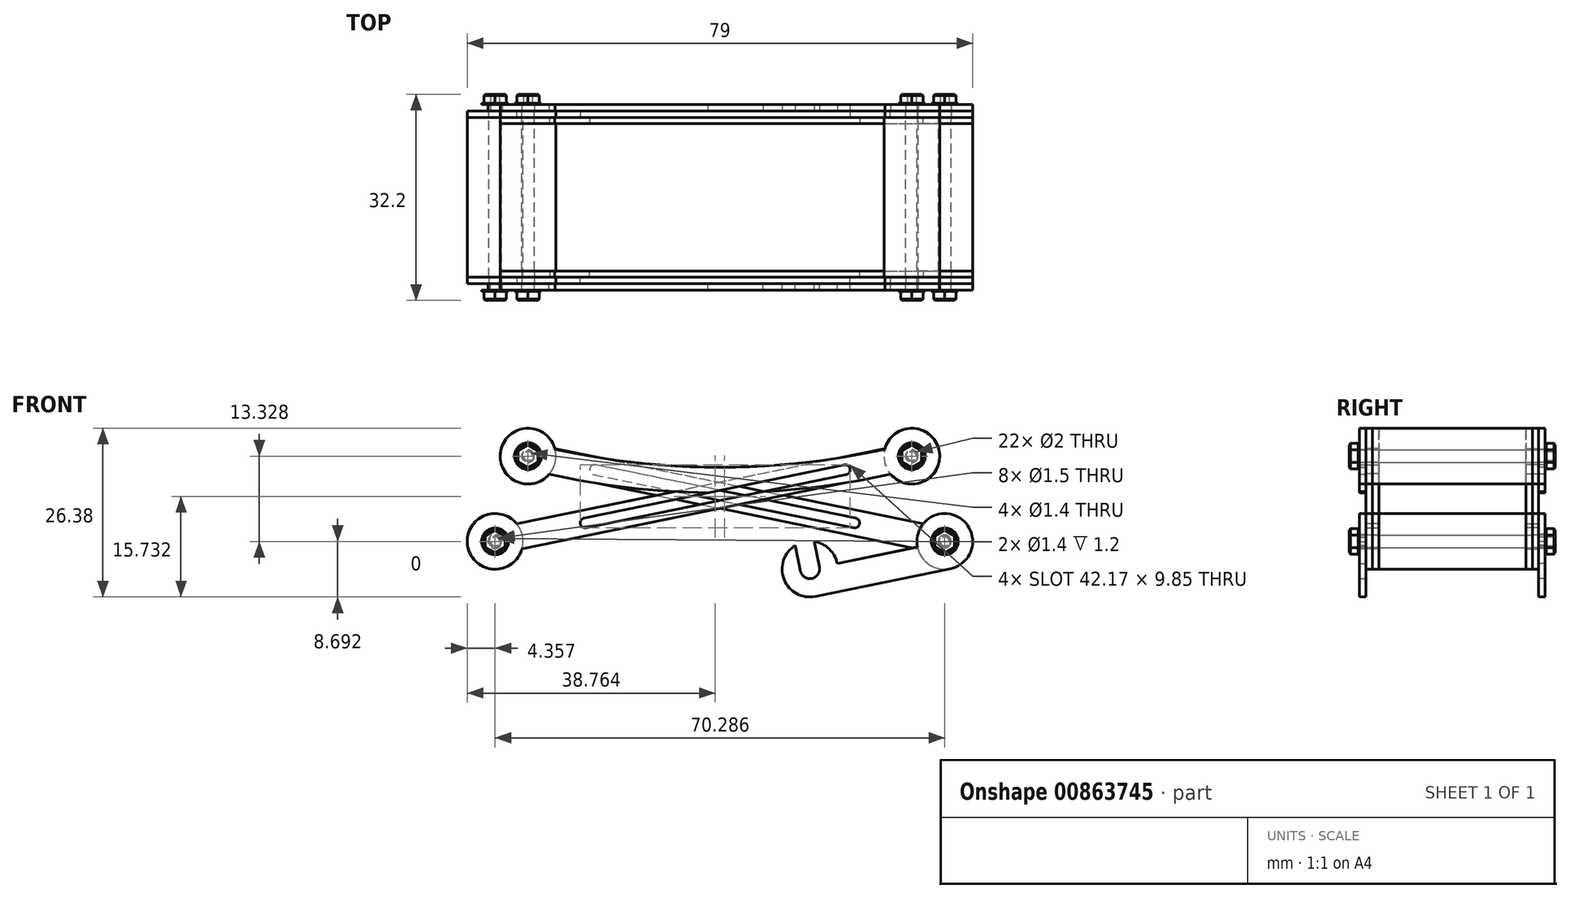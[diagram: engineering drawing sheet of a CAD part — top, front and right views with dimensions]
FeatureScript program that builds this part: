
annotation { "Feature Type Name" : "Feature", "Feature Type Description" : "" }
export const myFeature = defineFeature(function(context is Context, id is Id, definition is map)
    precondition{}
    {
        {
            var Q0;
            Q0=qCreatedBy(makeId("Front.planeOp"),FACE);
            var sketch = newSketch(context, id + "F0", { "sketchPlane" : qUnion([Q0])});
            skLineSegment(sketch, "E0", {"start": v(0, 0) * mm, "end": v(-30, 40) * mm, "construction": true});
            skLineSegment(sketch, "E1", {"start": v(-30, 40) * mm, "end": v(30, 40) * mm, "construction": true});
            skLineSegment(sketch, "E2", {"start": v(30, 40) * mm, "end": v(0, 0) * mm, "construction": true});
            skLineSegment(sketch, "E3", {"start": v(0, 0) * mm, "end": v(0, 40) * mm, "construction": true});
            skArc(sketch, "E4", {"start": v(-30, 40) * mm, "mid": v(0, 36.26) * mm, "end": v(30, 40) * mm, "construction": true});
            skPoint(sketch, "E4.third.point", {"position": v(0, 36.26) * mm});
            skLineSegment(sketch, "E5", {"start": v(30, 40) * mm, "end": v(-35.14, 26.67) * mm, "construction": true});
            skSolve(sketch);
        }
        {
            var Q0;
            Q0=qCreatedBy(makeId("Front.planeOp"),FACE);
            var sketch = newSketch(context, id + "F1", { "sketchPlane" : qUnion([Q0])});
            skArc(sketch, "E6", {"start": v(-25.77, 41.06) * mm, "mid": v(-34.24, 41) * mm, "end": v(-26.7, 37.16) * mm});
            skArc(sketch, "E7", {"start": v(26.7, 37.16) * mm, "mid": v(34.24, 41) * mm, "end": v(25.77, 41.06) * mm});
            skArc(sketch, "E8.0", {"start": v(-26.7, 37.16) * mm, "mid": v(0, 34.26) * mm, "end": v(26.7, 37.16) * mm});
            skArc(sketch, "E9.0", {"start": v(-25.77, 41.06) * mm, "mid": v(0, 38.26) * mm, "end": v(25.77, 41.06) * mm});
            skCircle(sketch, "E10", {"center": v(30, 40) * mm, "radius": 1 * mm});
            skCircle(sketch, "E11", {"center": v(-30, 40) * mm, "radius": 1 * mm});
            skSolve(sketch);
        }
        {
            var Q0;
            Q0=qCreatedBy(makeId("Front.planeOp"),FACE);
            var sketch = newSketch(context, id + "F2", { "sketchPlane" : qUnion([Q0])});
            skCircle(sketch, "E12", {"center": v(30, 40) * mm, "radius": 4.36 * mm});
            skLineSegment(sketch, "E13.0", {"start": v(29.6, 41.96) * mm, "end": v(-31.75, 29.4) * mm});
            skLineSegment(sketch, "E14.0", {"start": v(30.4, 38.04) * mm, "end": v(-30.95, 25.49) * mm});
            skArc(sketch, "E15", {"start": v(-31.75, 29.4) * mm, "mid": v(-39.41, 25.8) * mm, "end": v(-30.95, 25.49) * mm});
            skCircle(sketch, "E16", {"center": v(30, 40) * mm, "radius": 1 * mm});
            skCircle(sketch, "E17", {"center": v(-35.14, 26.67) * mm, "radius": 1 * mm});
            skSolve(sketch);
        }
        {
            var Q0;
            Q0 = qSketchRegion(id + "F2", true);
            extrude(context, id + "F3", {"entities" : qUnion([Q0]), "depth" : 1 * mm, "offsetDistance" : 25 * mm});
        }
        {
            var Q0;
            Q0 = qSketchRegion(id + "F1", true);
            extrude(context, id + "F4", {"entities" : qUnion([Q0]), "oppositeDirection" : true, "depth" : 1 * mm, "offsetDistance" : 25 * mm});
        }
        {
            var Q0;
            Q0=makeQuery(id+"F3.opExtrude","CAP_FACE",FACE,{"disambiguationData":[OSD([sQuery(id+"F2.wireOp",EDGE,"E12"),sQuery(id+"F2.wireOp",EDGE,"E13.0"),sQuery(id+"F2.wireOp",EDGE,"E14.0"),sQuery(id+"F2.wireOp",EDGE,"E15"),sQuery(id+"F2.wireOp",EDGE,"E16"),sQuery(id+"F2.wireOp",EDGE,"E17")])],"isStart":false});
            var sketch = newSketch(context, id + "F5", { "sketchPlane" : qUnion([Q0])});
            skCircle(sketch, "E18", {"center": v(30, 40) * mm, "radius": 4.36 * mm});
            skCircle(sketch, "E19", {"center": v(30, 40) * mm, "radius": 1 * mm});
            skCircle(sketch, "E20", {"center": v(-35.14, 26.67) * mm, "radius": 4.36 * mm});
            skCircle(sketch, "E21", {"center": v(-35.14, 26.67) * mm, "radius": 1 * mm});
            skSolve(sketch);
        }
        {
            var Q0;
            Q0 = qSketchRegion(id + "F5", true);
            extrude(context, id + "F6", {"entities" : qUnion([Q0]), "depth" : 25 * mm, "offsetDistance" : 25 * mm});
        }
        {
            var Q0;
            Q0=makeQuery(id+"F4.opExtrude","CAP_FACE",FACE,{"disambiguationData":[OSD([sQuery(id+"F1.wireOp",EDGE,"E6"),sQuery(id+"F1.wireOp",EDGE,"E7"),sQuery(id+"F1.wireOp",EDGE,"E8.0"),sQuery(id+"F1.wireOp",EDGE,"E9.0"),sQuery(id+"F1.wireOp",EDGE,"E10"),sQuery(id+"F1.wireOp",EDGE,"E11")])],"isStart":true});
            var sketch = newSketch(context, id + "F7", { "sketchPlane" : qUnion([Q0])});
            skCircle(sketch, "E22", {"center": v(-30, 40) * mm, "radius": 4.36 * mm});
            skCircle(sketch, "E23", {"center": v(-30, 40) * mm, "radius": 1 * mm});
            skSolve(sketch);
        }
        {
            var Q0;
            Q0 = qSketchRegion(id + "F7", true);
            extrude(context, id + "F8", {"entities" : qUnion([Q0]), "depth" : 1 * mm, "offsetDistance" : 25 * mm});
        }
        {
            var Q0;
            Q0=makeQuery(id+"F8.opExtrude","CAP_FACE",FACE,{"disambiguationData":[OSD([sQuery(id+"F7.wireOp",EDGE,"E22"),sQuery(id+"F7.wireOp",EDGE,"E23")])],"isStart":false});
            var sketch = newSketch(context, id + "F9", { "sketchPlane" : qUnion([Q0])});
            skSolve(sketch);
        }
        {
            var Q0;
            Q0=makeQuery(id+"F3.opExtrude","CAP_FACE",FACE,{"disambiguationData":[OSD([sQuery(id+"F2.wireOp",EDGE,"E12"),sQuery(id+"F2.wireOp",EDGE,"E13.0"),sQuery(id+"F2.wireOp",EDGE,"E14.0"),sQuery(id+"F2.wireOp",EDGE,"E15"),sQuery(id+"F2.wireOp",EDGE,"E16"),sQuery(id+"F2.wireOp",EDGE,"E17")])],"isStart":false});
            var sketch = newSketch(context, id + "F10", { "sketchPlane" : qUnion([Q0])});
            skLineSegment(sketch, "E24", {"start": v(-35.14, 26.67) * mm, "end": v(30, 40) * mm, "construction": true});
            skArc(sketch, "E25", {"start": v(-21.2, 30.32) * mm, "mid": v(-21.82, 29.4) * mm, "end": v(-20.9, 28.79) * mm});
            skArc(sketch, "E26", {"start": v(19.74, 37.1) * mm, "mid": v(20.35, 38.02) * mm, "end": v(19.42, 38.63) * mm});
            skLineSegment(sketch, "E27", {"start": v(-21.05, 29.56) * mm, "end": v(-0.74, 33.71) * mm, "construction": true});
            skLineSegment(sketch, "E28", {"start": v(-0.74, 33.71) * mm, "end": v(19.58, 37.87) * mm, "construction": true});
            skLineSegment(sketch, "E29", {"start": v(-21.2, 30.32) * mm, "end": v(19.42, 38.63) * mm});
            skLineSegment(sketch, "E30", {"start": v(19.74, 37.1) * mm, "end": v(-20.9, 28.79) * mm});
            skLineSegment(sketch, "E31", {"start": v(-21.2, 30.32) * mm, "end": v(-20.9, 28.79) * mm, "construction": true});
            skLineSegment(sketch, "E32", {"start": v(19.42, 38.63) * mm, "end": v(19.74, 37.1) * mm, "construction": true});
            skSolve(sketch);
        }
        {
            var Q0;
            Q0 = qSketchRegion(id + "F10", true);
            extrude(context, id + "F11", {"entities" : qUnion([Q0]), "operationType" : NewBodyOperationType.REMOVE, "oppositeDirection" : true, "depth" : 2 * mm, "offsetDistance" : 25 * mm});
        }
        {
            var Q0;
            Q0=makeQuery(id+"F3.opExtrude","SWEPT_BODY",BODY,{"disambiguationData":[OSD([sQuery(id+"F2.wireOp",EDGE,"E12"),sQuery(id+"F2.wireOp",EDGE,"E13.0"),sQuery(id+"F2.wireOp",EDGE,"E14.0"),sQuery(id+"F2.wireOp",EDGE,"E15"),sQuery(id+"F2.wireOp",EDGE,"E16"),sQuery(id+"F2.wireOp",EDGE,"E17")])]});
            var Q1;
            Q1=qCreatedBy(makeId("Right.planeOp"),FACE);
            mirror(context, id + "F12", {"entities" : qUnion([Q0]), "mirrorPlane" : qUnion([Q1])});
        }
        {
            var Q0;
            Q0=makeQuery(id+"F12.opPattern","COPY",BODY,{"derivedFrom":makeQuery(id+"F3.opExtrude","SWEPT_BODY",BODY,{"disambiguationData":[OSD([sQuery(id+"F2.wireOp",EDGE,"E12"),sQuery(id+"F2.wireOp",EDGE,"E13.0"),sQuery(id+"F2.wireOp",EDGE,"E14.0"),sQuery(id+"F2.wireOp",EDGE,"E15"),sQuery(id+"F2.wireOp",EDGE,"E16"),sQuery(id+"F2.wireOp",EDGE,"E17")])]}),"instanceName":"1"});
            var Q1;
            Q1=makeQuery(id+"F6.opExtrude","CAP_FACE",FACE,{"disambiguationData":[OSD([sQuery(id+"F5.wireOp",EDGE,"E20"),sQuery(id+"F5.wireOp",EDGE,"E21")])],"isStart":false});
            transform(context, id + "F13", {"entities" : qUnion([Q0]), "transformType" : TransformType.TRANSLATION_DISTANCE, "transformDirection" : qUnion([Q1]), "distance" : 1 * mm, "makeCopy" : false});
        }
        {
            var Q0;
            Q0=makeQuery(id+"F9.imprint","IMPRINT",FACE,{"disambiguationData":[TD([[makeQuery(id+"F9.imprint","IMPRINT",EDGE,{"derivedFrom":makeQuery(id+"F8.opExtrude","CAP_EDGE",EDGE,{"disambiguationData":[OSD([sQuery(id+"F7.wireOp",EDGE,"E22")])],"isStart":false})}),1.0]])]});
            extrude(context, id + "F14", {"entities" : qUnion([Q0]), "depth" : 24 * mm, "offsetDistance" : 25 * mm, "hasSecondDirection" : true, "secondDirectionOppositeDirection" : true, "secondDirectionDepth" : -1 * mm});
        }
        {
            var Q0;
            Q0=qCreatedBy(makeId("Front.planeOp"),FACE);
            cPlane(context, id + "F15", {"entities" : qUnion([Q0]), "cplaneType" : CPlaneType.OFFSET, "offset" : 13.5 * mm, "width" : 150 * mm, "height" : 150 * mm});
        }
        {
            var Q0;
            Q0=makeQuery(id+"F12.opPattern","COPY",BODY,{"derivedFrom":makeQuery(id+"F3.opExtrude","SWEPT_BODY",BODY,{"disambiguationData":[OSD([sQuery(id+"F2.wireOp",EDGE,"E12"),sQuery(id+"F2.wireOp",EDGE,"E13.0"),sQuery(id+"F2.wireOp",EDGE,"E14.0"),sQuery(id+"F2.wireOp",EDGE,"E15"),sQuery(id+"F2.wireOp",EDGE,"E16"),sQuery(id+"F2.wireOp",EDGE,"E17")])]}),"instanceName":"1"});
            var Q1;
            Q1=makeQuery(id+"F4.opExtrude","SWEPT_BODY",BODY,{"disambiguationData":[OSD([sQuery(id+"F1.wireOp",EDGE,"E6"),sQuery(id+"F1.wireOp",EDGE,"E7"),sQuery(id+"F1.wireOp",EDGE,"E8.0"),sQuery(id+"F1.wireOp",EDGE,"E9.0"),sQuery(id+"F1.wireOp",EDGE,"E10"),sQuery(id+"F1.wireOp",EDGE,"E11")])]});
            var Q2;
            Q2=makeQuery(id+"F8.opExtrude","SWEPT_BODY",BODY,{"disambiguationData":[OSD([sQuery(id+"F7.wireOp",EDGE,"E22"),sQuery(id+"F7.wireOp",EDGE,"E23")])]});
            var Q3;
            Q3=makeQuery(id+"F3.opExtrude","SWEPT_BODY",BODY,{"disambiguationData":[OSD([sQuery(id+"F2.wireOp",EDGE,"E12"),sQuery(id+"F2.wireOp",EDGE,"E13.0"),sQuery(id+"F2.wireOp",EDGE,"E14.0"),sQuery(id+"F2.wireOp",EDGE,"E15"),sQuery(id+"F2.wireOp",EDGE,"E16"),sQuery(id+"F2.wireOp",EDGE,"E17")])]});
            var Q4;
            Q4=qCreatedBy(id+"F15.planeOp",FACE);
            mirror(context, id + "F16", {"entities" : qUnion([Q0, Q1, Q2, Q3]), "mirrorPlane" : qUnion([Q4])});
        }
        {
            var Q0;
            Q0=makeQuery(id+"F12.opPattern","COPY",FACE,{"derivedFrom":makeQuery(id+"F3.opExtrude","CAP_FACE",FACE,{"disambiguationData":[OSD([sQuery(id+"F2.wireOp",EDGE,"E12"),sQuery(id+"F2.wireOp",EDGE,"E13.0"),sQuery(id+"F2.wireOp",EDGE,"E14.0"),sQuery(id+"F2.wireOp",EDGE,"E15"),sQuery(id+"F2.wireOp",EDGE,"E16"),sQuery(id+"F2.wireOp",EDGE,"E17")])],"isStart":false}),"instanceName":"1"});
            var sketch = newSketch(context, id + "F17", { "sketchPlane" : qUnion([Q0])});
            skCircle(sketch, "E33", {"center": v(35.14, 26.67) * mm, "radius": 4.36 * mm});
            skCircle(sketch, "E34", {"center": v(35.14, 26.67) * mm, "radius": 1 * mm});
            skSolve(sketch);
        }
        {
            var Q0;
            Q0 = qSketchRegion(id + "F17", true);
            var Q1;
            Q1=makeQuery(id+"F16.opPattern","COPY",FACE,{"derivedFrom":makeQuery(id+"F12.opPattern","COPY",FACE,{"derivedFrom":makeQuery(id+"F3.opExtrude","CAP_FACE",FACE,{"disambiguationData":[OSD([sQuery(id+"F2.wireOp",EDGE,"E12"),sQuery(id+"F2.wireOp",EDGE,"E13.0"),sQuery(id+"F2.wireOp",EDGE,"E14.0"),sQuery(id+"F2.wireOp",EDGE,"E15"),sQuery(id+"F2.wireOp",EDGE,"E16"),sQuery(id+"F2.wireOp",EDGE,"E17")])],"isStart":false}),"instanceName":"1"}),"instanceName":"1"});
            extrude(context, id + "F18", {"entities" : qUnion([Q0]), "endBound" : BoundingType.UP_TO_SURFACE, "depth" : 25 * mm, "endBoundEntityFace" : qUnion([Q1]), "offsetDistance" : 25 * mm});
        }
        {
            var Q0;
            Q0=makeQuery(id+"F12.opPattern","COPY",FACE,{"derivedFrom":makeQuery(id+"F3.opExtrude","CAP_FACE",FACE,{"disambiguationData":[OSD([sQuery(id+"F2.wireOp",EDGE,"E12"),sQuery(id+"F2.wireOp",EDGE,"E13.0"),sQuery(id+"F2.wireOp",EDGE,"E14.0"),sQuery(id+"F2.wireOp",EDGE,"E15"),sQuery(id+"F2.wireOp",EDGE,"E16"),sQuery(id+"F2.wireOp",EDGE,"E17")])],"isStart":true}),"instanceName":"1"});
            var sketch = newSketch(context, id + "F19", { "sketchPlane" : qUnion([Q0])});
            skCircle(sketch, "E35", {"center": v(-35.14, 26.67) * mm, "radius": 4.36 * mm});
            skCircle(sketch, "E36", {"center": v(-35.14, 26.67) * mm, "radius": 1 * mm});
            skSolve(sketch);
        }
        {
            var Q0;
            Q0 = qSketchRegion(id + "F19", true);
            extrude(context, id + "F20", {"entities" : qUnion([Q0]), "depth" : 1 * mm, "offsetDistance" : 25 * mm});
        }
        {
            var Q0;
            Q0=makeQuery(id+"F20.opExtrude","SWEPT_BODY",BODY,{"disambiguationData":[OSD([sQuery(id+"F19.wireOp",EDGE,"E35"),sQuery(id+"F19.wireOp",EDGE,"E36")])]});
            var Q1;
            Q1=qCreatedBy(id+"F15.planeOp",FACE);
            mirror(context, id + "F21", {"entities" : qUnion([Q0]), "mirrorPlane" : qUnion([Q1])});
        }
        {
            var Q0;
            Q0=makeQuery(id+"F21.opPattern","COPY",FACE,{"derivedFrom":makeQuery(id+"F20.opExtrude","CAP_FACE",FACE,{"disambiguationData":[OSD([sQuery(id+"F19.wireOp",EDGE,"E35"),sQuery(id+"F19.wireOp",EDGE,"E36")])],"isStart":false}),"instanceName":"1"});
            var sketch = newSketch(context, id + "F22", { "sketchPlane" : qUnion([Q0])});
            skArc(sketch, "E37", {"start": v(36.02, 22.4) * mm, "mid": v(37.54, 30.31) * mm, "end": v(30.88, 25.8) * mm});
            skLineSegment(sketch, "E38", {"start": v(35.14, 26.67) * mm, "end": v(36.02, 22.4) * mm, "construction": true});
            skLineSegment(sketch, "E39", {"start": v(36.02, 22.4) * mm, "end": v(14.96, 18.07) * mm, "construction": true});
            skLineSegment(sketch, "E40", {"start": v(35.14, 26.67) * mm, "end": v(14.08, 22.34) * mm, "construction": true});
            skLineSegment(sketch, "E41", {"start": v(14.08, 22.34) * mm, "end": v(14.96, 18.07) * mm, "construction": true});
            skArc(sketch, "E42", {"start": v(11.78, 26.04) * mm, "mid": v(10.03, 20.73) * mm, "end": v(14.96, 18.07) * mm});
            skArc(sketch, "E43", {"start": v(12.6, 22.04) * mm, "mid": v(14.38, 20.87) * mm, "end": v(15.55, 22.64) * mm});
            skLineSegment(sketch, "E44", {"start": v(15.55, 22.64) * mm, "end": v(14.72, 26.65) * mm});
            skLineSegment(sketch, "E45", {"start": v(12.6, 22.04) * mm, "end": v(11.78, 26.04) * mm});
            skLineSegment(sketch, "E46", {"start": v(11.78, 26.04) * mm, "end": v(14.72, 26.65) * mm, "construction": true});
            skLineSegment(sketch, "E47", {"start": v(14.08, 22.34) * mm, "end": v(12.6, 22.04) * mm, "construction": true});
            skArc(sketch, "E48.trimOffspring", {"start": v(18.35, 23.22) * mm, "mid": v(17.07, 25.5) * mm, "end": v(14.72, 26.65) * mm});
            skLineSegment(sketch, "E49", {"start": v(18.35, 23.22) * mm, "end": v(30.88, 25.8) * mm});
            skLineSegment(sketch, "E50", {"start": v(14.96, 18.07) * mm, "end": v(36.02, 22.4) * mm});
            skCircle(sketch, "E51", {"center": v(35.14, 26.67) * mm, "radius": 1 * mm});
            skSolve(sketch);
        }
        {
            var Q0;
            Q0 = qSketchRegion(id + "F22", true);
            extrude(context, id + "F23", {"entities" : qUnion([Q0]), "depth" : 1 * mm, "offsetDistance" : 25 * mm});
        }
        {
            var Q0;
            Q0=makeQuery(id+"F23.opExtrude","SWEPT_BODY",BODY,{"disambiguationData":[OSD([sQuery(id+"F22.wireOp",EDGE,"E37"),sQuery(id+"F22.wireOp",EDGE,"E42"),sQuery(id+"F22.wireOp",EDGE,"E43"),sQuery(id+"F22.wireOp",EDGE,"E44"),sQuery(id+"F22.wireOp",EDGE,"E45"),sQuery(id+"F22.wireOp",EDGE,"E48.trimOffspring"),sQuery(id+"F22.wireOp",EDGE,"E49"),sQuery(id+"F22.wireOp",EDGE,"E50"),sQuery(id+"F22.wireOp",EDGE,"E51")])]});
            var Q1;
            Q1=qCreatedBy(id+"F15.planeOp",FACE);
            mirror(context, id + "F24", {"entities" : qUnion([Q0]), "mirrorPlane" : qUnion([Q1])});
        }
        {
            var Q0;
            Q0=makeQuery(id+"F16.opPattern","COPY",FACE,{"derivedFrom":makeQuery(id+"F4.opExtrude","CAP_FACE",FACE,{"disambiguationData":[OSD([sQuery(id+"F1.wireOp",EDGE,"E6"),sQuery(id+"F1.wireOp",EDGE,"E7"),sQuery(id+"F1.wireOp",EDGE,"E8.0"),sQuery(id+"F1.wireOp",EDGE,"E9.0"),sQuery(id+"F1.wireOp",EDGE,"E10"),sQuery(id+"F1.wireOp",EDGE,"E11")])],"isStart":false}),"instanceName":"1"});
            var sketch = newSketch(context, id + "F25", { "sketchPlane" : qUnion([Q0])});
            skCircle(sketch, "E52.cCircle", {"center": v(30, 40) * mm, "radius": 2 * mm, "construction": true});
            skLineSegment(sketch, "E52.0", {"start": v(30, 42) * mm, "end": v(31.74, 41) * mm});
            skLineSegment(sketch, "E52.1", {"start": v(31.74, 41) * mm, "end": v(31.73, 39) * mm});
            skLineSegment(sketch, "E52.2", {"start": v(31.73, 39) * mm, "end": v(30, 38) * mm});
            skLineSegment(sketch, "E52.3", {"start": v(30, 38) * mm, "end": v(28.26, 39) * mm});
            skLineSegment(sketch, "E52.4", {"start": v(28.26, 39) * mm, "end": v(28.27, 41) * mm});
            skLineSegment(sketch, "E52.5", {"start": v(28.27, 41) * mm, "end": v(30, 42) * mm});
            skCircle(sketch, "E53.cCircle", {"center": v(35.14, 26.67) * mm, "radius": 2 * mm, "construction": true});
            skLineSegment(sketch, "E53.0", {"start": v(35.15, 28.67) * mm, "end": v(36.88, 27.67) * mm});
            skLineSegment(sketch, "E53.1", {"start": v(36.88, 27.67) * mm, "end": v(36.87, 25.67) * mm});
            skLineSegment(sketch, "E53.2", {"start": v(36.87, 25.67) * mm, "end": v(35.14, 24.67) * mm});
            skLineSegment(sketch, "E53.3", {"start": v(35.14, 24.67) * mm, "end": v(33.4, 25.68) * mm});
            skLineSegment(sketch, "E53.4", {"start": v(33.4, 25.68) * mm, "end": v(33.41, 27.68) * mm});
            skLineSegment(sketch, "E53.5", {"start": v(33.41, 27.68) * mm, "end": v(35.15, 28.67) * mm});
            skSolve(sketch);
        }
        {
            var Q0;
            Q0 = qSketchRegion(id + "F25", true);
            extrude(context, id + "F26", {"entities" : qUnion([Q0]), "depth" : 1.6 * mm, "offsetDistance" : 25 * mm, "hasSecondDirection" : true, "secondDirectionOppositeDirection" : false, "secondDirectionDepth" : .2 * mm});
        }
        {
            var Q0;
            Q0=makeQuery(id+"F26.opExtrude","CAP_EDGE",EDGE,{"disambiguationData":[OSD([sQuery(id+"F25.wireOp",EDGE,"E52.2")])],"isStart":false});
            var Q1;
            Q1=makeQuery(id+"F26.opExtrude","CAP_EDGE",EDGE,{"disambiguationData":[OSD([sQuery(id+"F25.wireOp",EDGE,"E52.1")])],"isStart":false});
            var Q2;
            Q2=makeQuery(id+"F26.opExtrude","CAP_EDGE",EDGE,{"disambiguationData":[OSD([sQuery(id+"F25.wireOp",EDGE,"E52.0")])],"isStart":false});
            var Q3;
            Q3=makeQuery(id+"F26.opExtrude","CAP_EDGE",EDGE,{"disambiguationData":[OSD([sQuery(id+"F25.wireOp",EDGE,"E52.5")])],"isStart":false});
            var Q4;
            Q4=makeQuery(id+"F26.opExtrude","CAP_EDGE",EDGE,{"disambiguationData":[OSD([sQuery(id+"F25.wireOp",EDGE,"E52.4")])],"isStart":false});
            var Q5;
            Q5=makeQuery(id+"F26.opExtrude","CAP_EDGE",EDGE,{"disambiguationData":[OSD([sQuery(id+"F25.wireOp",EDGE,"E52.3")])],"isStart":false});
            var Q6;
            Q6=makeQuery(id+"F26.opExtrude","CAP_EDGE",EDGE,{"disambiguationData":[OSD([sQuery(id+"F25.wireOp",EDGE,"E53.0")])],"isStart":false});
            var Q7;
            Q7=makeQuery(id+"F26.opExtrude","CAP_EDGE",EDGE,{"disambiguationData":[OSD([sQuery(id+"F25.wireOp",EDGE,"E53.5")])],"isStart":false});
            var Q8;
            Q8=makeQuery(id+"F26.opExtrude","CAP_EDGE",EDGE,{"disambiguationData":[OSD([sQuery(id+"F25.wireOp",EDGE,"E53.4")])],"isStart":false});
            var Q9;
            Q9=makeQuery(id+"F26.opExtrude","CAP_EDGE",EDGE,{"disambiguationData":[OSD([sQuery(id+"F25.wireOp",EDGE,"E53.3")])],"isStart":false});
            var Q10;
            Q10=makeQuery(id+"F26.opExtrude","CAP_EDGE",EDGE,{"disambiguationData":[OSD([sQuery(id+"F25.wireOp",EDGE,"E53.2")])],"isStart":false});
            var Q11;
            Q11=makeQuery(id+"F26.opExtrude","CAP_EDGE",EDGE,{"disambiguationData":[OSD([sQuery(id+"F25.wireOp",EDGE,"E53.1")])],"isStart":false});
            chamfer(context, id + "F27", {"entities" : qUnion([Q0, Q1, Q2, Q3, Q4, Q5, Q6, Q7, Q8, Q9, Q10, Q11]), "width" : .2 * mm, "tangentPropagation" : true});
        }
        {
            var Q0;
            Q0=makeQuery(id+"F26.opExtrude","SWEPT_BODY",BODY,{"disambiguationData":[OSD([sQuery(id+"F25.wireOp",EDGE,"E52.0"),sQuery(id+"F25.wireOp",EDGE,"E52.1"),sQuery(id+"F25.wireOp",EDGE,"E52.2"),sQuery(id+"F25.wireOp",EDGE,"E52.3"),sQuery(id+"F25.wireOp",EDGE,"E52.4"),sQuery(id+"F25.wireOp",EDGE,"E52.5")])]});
            var Q1;
            Q1=makeQuery(id+"F26.opExtrude","SWEPT_BODY",BODY,{"disambiguationData":[OSD([sQuery(id+"F25.wireOp",EDGE,"E53.0"),sQuery(id+"F25.wireOp",EDGE,"E53.1"),sQuery(id+"F25.wireOp",EDGE,"E53.2"),sQuery(id+"F25.wireOp",EDGE,"E53.3"),sQuery(id+"F25.wireOp",EDGE,"E53.4"),sQuery(id+"F25.wireOp",EDGE,"E53.5")])]});
            var Q2;
            Q2=qCreatedBy(id+"F15.planeOp",FACE);
            mirror(context, id + "F28", {"entities" : qUnion([Q0, Q1]), "mirrorPlane" : qUnion([Q2])});
        }
        {
            var Q0;
            Q0=makeQuery(id+"F4.opExtrude","CAP_FACE",FACE,{"disambiguationData":[OSD([sQuery(id+"F1.wireOp",EDGE,"E6"),sQuery(id+"F1.wireOp",EDGE,"E7"),sQuery(id+"F1.wireOp",EDGE,"E8.0"),sQuery(id+"F1.wireOp",EDGE,"E9.0"),sQuery(id+"F1.wireOp",EDGE,"E10"),sQuery(id+"F1.wireOp",EDGE,"E11")])],"isStart":false});
            var sketch = newSketch(context, id + "F29", { "sketchPlane" : qUnion([Q0])});
            skCircle(sketch, "E54", {"center": v(-30, 40) * mm, "radius": 0.7 * mm});
            skCircle(sketch, "E55", {"center": v(-35.14, 26.67) * mm, "radius": 0.7 * mm});
            skSolve(sketch);
        }
        {
            var Q0;
            Q0 = qSketchRegion(id + "F29", true);
            extrude(context, id + "F30", {"entities" : qUnion([Q0]), "operationType" : NewBodyOperationType.REMOVE, "depth" : 25 * mm, "offsetDistance" : 25 * mm});
        }
        {
            var Q0;
            Q0=makeQuery(id+"F30.boolean.opBoolean","INTERSECT",EDGE,{"derivedFrom":[makeQuery(id+"F28.opPattern","COPY",FACE,{"derivedFrom":makeQuery(id+"F26.opExtrude","CAP_FACE",FACE,{"disambiguationData":[OSD([sQuery(id+"F25.wireOp",EDGE,"E52.0"),sQuery(id+"F25.wireOp",EDGE,"E52.1"),sQuery(id+"F25.wireOp",EDGE,"E52.2"),sQuery(id+"F25.wireOp",EDGE,"E52.3"),sQuery(id+"F25.wireOp",EDGE,"E52.4"),sQuery(id+"F25.wireOp",EDGE,"E52.5")])],"isStart":false}),"instanceName":"1"}),makeQuery(id+"F30.opExtrude","SWEPT_FACE",FACE,{"disambiguationData":[OSD([sQuery(id+"F29.wireOp",EDGE,"E54")])]})]});
            var Q1;
            Q1=makeQuery(id+"F30.boolean.opBoolean","INTERSECT",EDGE,{"derivedFrom":[makeQuery(id+"F28.opPattern","COPY",FACE,{"derivedFrom":makeQuery(id+"F26.opExtrude","CAP_FACE",FACE,{"disambiguationData":[OSD([sQuery(id+"F25.wireOp",EDGE,"E53.0"),sQuery(id+"F25.wireOp",EDGE,"E53.1"),sQuery(id+"F25.wireOp",EDGE,"E53.2"),sQuery(id+"F25.wireOp",EDGE,"E53.3"),sQuery(id+"F25.wireOp",EDGE,"E53.4"),sQuery(id+"F25.wireOp",EDGE,"E53.5")])],"isStart":false}),"instanceName":"1"}),makeQuery(id+"F30.opExtrude","SWEPT_FACE",FACE,{"disambiguationData":[OSD([sQuery(id+"F29.wireOp",EDGE,"E55")])]})]});
            chamfer(context, id + "F31", {"entities" : qUnion([Q0, Q1]), "width" : .2 * mm, "tangentPropagation" : true});
        }
        {
            var Q0;
            Q0=makeQuery(id+"F16.opPattern","COPY",FACE,{"derivedFrom":makeQuery(id+"F4.opExtrude","CAP_FACE",FACE,{"disambiguationData":[OSD([sQuery(id+"F1.wireOp",EDGE,"E6"),sQuery(id+"F1.wireOp",EDGE,"E7"),sQuery(id+"F1.wireOp",EDGE,"E8.0"),sQuery(id+"F1.wireOp",EDGE,"E9.0"),sQuery(id+"F1.wireOp",EDGE,"E10"),sQuery(id+"F1.wireOp",EDGE,"E11")])],"isStart":false}),"instanceName":"1"});
            var sketch = newSketch(context, id + "F32", { "sketchPlane" : qUnion([Q0])});
            skCircle(sketch, "E56", {"center": v(30, 40) * mm, "radius": 2.1 * mm});
            skCircle(sketch, "E57", {"center": v(30, 40) * mm, "radius": 0.75 * mm});
            skCircle(sketch, "E58", {"center": v(35.14, 26.67) * mm, "radius": 2.1 * mm});
            skCircle(sketch, "E59", {"center": v(35.14, 26.67) * mm, "radius": 0.75 * mm});
            skSolve(sketch);
        }
        {
            var Q0;
            Q0 = qSketchRegion(id + "F32", true);
            var Q1;
            Q1=makeQuery(id+"F26.opExtrude","CAP_FACE",FACE,{"disambiguationData":[OSD([sQuery(id+"F25.wireOp",EDGE,"E52.0"),sQuery(id+"F25.wireOp",EDGE,"E52.1"),sQuery(id+"F25.wireOp",EDGE,"E52.2"),sQuery(id+"F25.wireOp",EDGE,"E52.3"),sQuery(id+"F25.wireOp",EDGE,"E52.4"),sQuery(id+"F25.wireOp",EDGE,"E52.5")])],"isStart":true});
            extrude(context, id + "F33", {"entities" : qUnion([Q0]), "endBound" : BoundingType.UP_TO_SURFACE, "depth" : 25 * mm, "endBoundEntityFace" : qUnion([Q1]), "offsetDistance" : 25 * mm});
        }
        {
            var Q0;
            Q0=makeQuery(id+"F33.opExtrude","SWEPT_BODY",BODY,{"disambiguationData":[OSD([sQuery(id+"F32.wireOp",EDGE,"E56"),sQuery(id+"F32.wireOp",EDGE,"E57")])]});
            var Q1;
            Q1=makeQuery(id+"F33.opExtrude","SWEPT_BODY",BODY,{"disambiguationData":[OSD([sQuery(id+"F32.wireOp",EDGE,"E58"),sQuery(id+"F32.wireOp",EDGE,"E59")])]});
            var Q2;
            Q2=qCreatedBy(id+"F15.planeOp",FACE);
            mirror(context, id + "F34", {"entities" : qUnion([Q0, Q1]), "mirrorPlane" : qUnion([Q2])});
        }
        {
            var Q0;
            Q0=makeQuery(id+"F26.opExtrude","SWEPT_BODY",BODY,{"disambiguationData":[OSD([sQuery(id+"F25.wireOp",EDGE,"E52.0"),sQuery(id+"F25.wireOp",EDGE,"E52.1"),sQuery(id+"F25.wireOp",EDGE,"E52.2"),sQuery(id+"F25.wireOp",EDGE,"E52.3"),sQuery(id+"F25.wireOp",EDGE,"E52.4"),sQuery(id+"F25.wireOp",EDGE,"E52.5")])]});
            var Q1;
            Q1=makeQuery(id+"F33.opExtrude","SWEPT_BODY",BODY,{"disambiguationData":[OSD([sQuery(id+"F32.wireOp",EDGE,"E56"),sQuery(id+"F32.wireOp",EDGE,"E57")])]});
            var Q2;
            Q2=makeQuery(id+"F26.opExtrude","SWEPT_BODY",BODY,{"disambiguationData":[OSD([sQuery(id+"F25.wireOp",EDGE,"E53.0"),sQuery(id+"F25.wireOp",EDGE,"E53.1"),sQuery(id+"F25.wireOp",EDGE,"E53.2"),sQuery(id+"F25.wireOp",EDGE,"E53.3"),sQuery(id+"F25.wireOp",EDGE,"E53.4"),sQuery(id+"F25.wireOp",EDGE,"E53.5")])]});
            var Q3;
            Q3=makeQuery(id+"F33.opExtrude","SWEPT_BODY",BODY,{"disambiguationData":[OSD([sQuery(id+"F32.wireOp",EDGE,"E58"),sQuery(id+"F32.wireOp",EDGE,"E59")])]});
            var Q4;
            Q4=makeQuery(id+"F34.opPattern","COPY",BODY,{"derivedFrom":makeQuery(id+"F33.opExtrude","SWEPT_BODY",BODY,{"disambiguationData":[OSD([sQuery(id+"F32.wireOp",EDGE,"E58"),sQuery(id+"F32.wireOp",EDGE,"E59")])]}),"instanceName":"1"});
            var Q5;
            Q5=makeQuery(id+"F28.opPattern","COPY",BODY,{"derivedFrom":makeQuery(id+"F26.opExtrude","SWEPT_BODY",BODY,{"disambiguationData":[OSD([sQuery(id+"F25.wireOp",EDGE,"E53.0"),sQuery(id+"F25.wireOp",EDGE,"E53.1"),sQuery(id+"F25.wireOp",EDGE,"E53.2"),sQuery(id+"F25.wireOp",EDGE,"E53.3"),sQuery(id+"F25.wireOp",EDGE,"E53.4"),sQuery(id+"F25.wireOp",EDGE,"E53.5")])]}),"instanceName":"1"});
            var Q6;
            Q6=makeQuery(id+"F28.opPattern","COPY",BODY,{"derivedFrom":makeQuery(id+"F26.opExtrude","SWEPT_BODY",BODY,{"disambiguationData":[OSD([sQuery(id+"F25.wireOp",EDGE,"E52.0"),sQuery(id+"F25.wireOp",EDGE,"E52.1"),sQuery(id+"F25.wireOp",EDGE,"E52.2"),sQuery(id+"F25.wireOp",EDGE,"E52.3"),sQuery(id+"F25.wireOp",EDGE,"E52.4"),sQuery(id+"F25.wireOp",EDGE,"E52.5")])]}),"instanceName":"1"});
            var Q7;
            Q7=makeQuery(id+"F34.opPattern","COPY",BODY,{"derivedFrom":makeQuery(id+"F33.opExtrude","SWEPT_BODY",BODY,{"disambiguationData":[OSD([sQuery(id+"F32.wireOp",EDGE,"E56"),sQuery(id+"F32.wireOp",EDGE,"E57")])]}),"instanceName":"1"});
            var Q8;
            Q8=qCreatedBy(makeId("Right.planeOp"),FACE);
            mirror(context, id + "F35", {"entities" : qUnion([Q0, Q1, Q2, Q3, Q4, Q5, Q6, Q7]), "mirrorPlane" : qUnion([Q8])});
        }
        {
            var Q0;
            Q0=makeQuery(id+"F3.opExtrude","CAP_FACE",FACE,{"disambiguationData":[OSD([sQuery(id+"F2.wireOp",EDGE,"E12"),sQuery(id+"F2.wireOp",EDGE,"E13.0"),sQuery(id+"F2.wireOp",EDGE,"E14.0"),sQuery(id+"F2.wireOp",EDGE,"E15"),sQuery(id+"F2.wireOp",EDGE,"E16"),sQuery(id+"F2.wireOp",EDGE,"E17")])],"isStart":true});
            var sketch = newSketch(context, id + "F36", { "sketchPlane" : qUnion([Q0])});
            skCircle(sketch, "E60", {"center": v(35.14, 26.67) * mm, "radius": 0.7 * mm});
            skCircle(sketch, "E61", {"center": v(35.14, 26.67) * mm, "radius": 1.1 * mm});
            skSolve(sketch);
        }
        {
            var Q0;
            Q0 = qSketchRegion(id + "F36", true);
            var Q1;
            Q1=makeQuery(id+"F35.opPattern","COPY",FACE,{"derivedFrom":makeQuery(id+"F28.opPattern","COPY",FACE,{"derivedFrom":makeQuery(id+"F26.opExtrude","CAP_FACE",FACE,{"disambiguationData":[OSD([sQuery(id+"F25.wireOp",EDGE,"E53.0"),sQuery(id+"F25.wireOp",EDGE,"E53.1"),sQuery(id+"F25.wireOp",EDGE,"E53.2"),sQuery(id+"F25.wireOp",EDGE,"E53.3"),sQuery(id+"F25.wireOp",EDGE,"E53.4"),sQuery(id+"F25.wireOp",EDGE,"E53.5")])],"isStart":true}),"instanceName":"1"}),"instanceName":"1"});
            extrude(context, id + "F37", {"entities" : qUnion([Q0]), "endBound" : BoundingType.UP_TO_SURFACE, "depth" : 25 * mm, "endBoundEntityFace" : qUnion([Q1]), "offsetDistance" : 25 * mm});
        }
        {
            var Q0;
            Q0=makeQuery(id+"F37.opExtrude","SWEPT_BODY",BODY,{"disambiguationData":[OSD([sQuery(id+"F36.wireOp",EDGE,"E60"),sQuery(id+"F36.wireOp",EDGE,"E61")])]});
            var Q1;
            Q1=qCreatedBy(id+"F15.planeOp",FACE);
            mirror(context, id + "F38", {"entities" : qUnion([Q0]), "mirrorPlane" : qUnion([Q1])});
        }
    });
